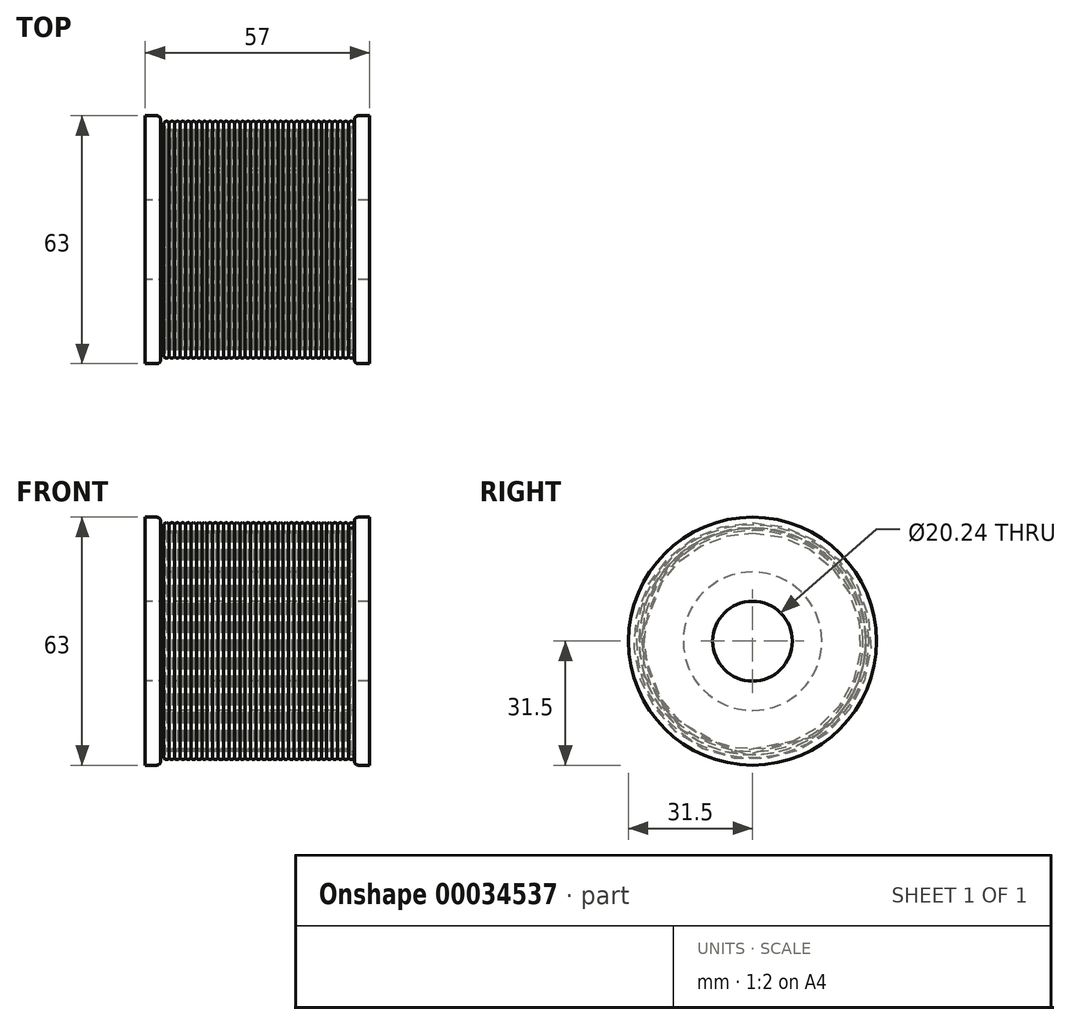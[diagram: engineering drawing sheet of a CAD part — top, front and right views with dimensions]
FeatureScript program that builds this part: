
annotation { "Feature Type Name" : "Feature", "Feature Type Description" : "" }
export const myFeature = defineFeature(function(context is Context, id is Id, definition is map)
    precondition{}
    {
        {
            var Q0;
            Q0=qCreatedBy(makeId("Front.planeOp"),FACE);
            var sketch = newSketch(context, id + "F0", { "sketchPlane" : qUnion([Q0])});
            skLineSegment(sketch, "E0", {"start": v(0, 17.6) * mm, "end": v(24.6, 17.6) * mm});
            skLineSegment(sketch, "E1", {"start": v(24.6, 17.6) * mm, "end": v(24.6, 31.5) * mm});
            skLineSegment(sketch, "E2", {"start": v(24.6, 31.5) * mm, "end": v(28.5, 31.5) * mm});
            skLineSegment(sketch, "E3", {"start": v(28.5, 31.5) * mm, "end": v(28.5, 10.12) * mm});
            skLineSegment(sketch, "E4", {"start": v(28.5, 10.12) * mm, "end": v(0, 10.12) * mm});
            skLineSegment(sketch, "E5.MirrorCS", {"start": v(0, 17.6) * mm, "end": v(-24.6, 17.6) * mm});
            skLineSegment(sketch, "E6.MirrorCS", {"start": v(-28.5, 10.12) * mm, "end": v(0, 10.12) * mm});
            skLineSegment(sketch, "E7.MirrorCS", {"start": v(-28.5, 31.5) * mm, "end": v(-28.5, 10.12) * mm});
            skLineSegment(sketch, "E8.MirrorCS", {"start": v(-24.6, 17.6) * mm, "end": v(-24.6, 31.5) * mm});
            skLineSegment(sketch, "E9.MirrorCS", {"start": v(-24.6, 31.5) * mm, "end": v(-28.5, 31.5) * mm});
            skLineSegment(sketch, "E10", {"start": v(-37.64, 0) * mm, "end": v(50.45, 0) * mm, "construction": true});
            skPoint(sketch, "E11.first.point", {"position": v(-22.46, 29.65) * mm});
            skPoint(sketch, "E11.second.point", {"position": v(-22.46, 29.64) * mm});
            skPoint(sketch, "E11.third.point", {"position": v(-22.63, 29.9) * mm});
            skArc(sketch, "E12.1.0.0", {"start": v(-21.05, 29.52) * mm, "mid": v(-21.74, 30.1) * mm, "end": v(-22.43, 29.52) * mm});
            skArc(sketch, "E12.2.0.0", {"start": v(-19.67, 29.52) * mm, "mid": v(-20.36, 30.1) * mm, "end": v(-21.05, 29.52) * mm});
            skArc(sketch, "E12.3.0.0", {"start": v(-18.29, 29.52) * mm, "mid": v(-18.98, 30.1) * mm, "end": v(-19.67, 29.52) * mm});
            skArc(sketch, "E12.4.0.0", {"start": v(-16.9, 29.52) * mm, "mid": v(-17.6, 30.1) * mm, "end": v(-18.29, 29.52) * mm});
            skArc(sketch, "E12.6.0.0", {"start": v(-14.15, 29.52) * mm, "mid": v(-14.84, 30.1) * mm, "end": v(-15.53, 29.52) * mm});
            skArc(sketch, "E12.7.0.0", {"start": v(-12.77, 29.52) * mm, "mid": v(-13.46, 30.1) * mm, "end": v(-14.15, 29.52) * mm});
            skArc(sketch, "E12.8.0.0", {"start": v(-11.39, 29.52) * mm, "mid": v(-12.08, 30.1) * mm, "end": v(-12.77, 29.52) * mm});
            skArc(sketch, "E12.9.0.0", {"start": v(-10, 29.52) * mm, "mid": v(-10.7, 30.1) * mm, "end": v(-11.39, 29.52) * mm});
            skArc(sketch, "E12.10.0.0", {"start": v(-8.63, 29.52) * mm, "mid": v(-9.32, 30.1) * mm, "end": v(-10, 29.52) * mm});
            skArc(sketch, "E12.11.0.0", {"start": v(-7.25, 29.52) * mm, "mid": v(-7.94, 30.1) * mm, "end": v(-8.63, 29.52) * mm});
            skArc(sketch, "E12.12.0.0", {"start": v(-5.87, 29.52) * mm, "mid": v(-6.56, 30.1) * mm, "end": v(-7.25, 29.52) * mm});
            skArc(sketch, "E12.13.0.0", {"start": v(-4.49, 29.52) * mm, "mid": v(-5.18, 30.1) * mm, "end": v(-5.87, 29.52) * mm});
            skArc(sketch, "E12.14.0.0", {"start": v(-3.1, 29.52) * mm, "mid": v(-3.8, 30.1) * mm, "end": v(-4.49, 29.52) * mm});
            skArc(sketch, "E12.15.0.0", {"start": v(-1.73, 29.52) * mm, "mid": v(-2.42, 30.1) * mm, "end": v(-3.1, 29.52) * mm});
            skArc(sketch, "E12.16.0.0", {"start": v(-0.35, 29.52) * mm, "mid": v(-1.04, 30.1) * mm, "end": v(-1.73, 29.52) * mm});
            skArc(sketch, "E12.17.0.0", {"start": v(1.03, 29.52) * mm, "mid": v(0.34, 30.1) * mm, "end": v(-0.35, 29.52) * mm});
            skArc(sketch, "E12.18.0.0", {"start": v(2.41, 29.52) * mm, "mid": v(1.72, 30.1) * mm, "end": v(1.03, 29.52) * mm});
            skArc(sketch, "E12.19.0.0", {"start": v(3.8, 29.52) * mm, "mid": v(3.1, 30.1) * mm, "end": v(2.41, 29.52) * mm});
            skLineSegment(sketch, "E12.direction1", {"start": v(-23.12, 29.4) * mm, "end": v(-21.74, 29.4) * mm, "construction": true});
            skArc(sketch, "E13.0.20.0", {"start": v(5.17, 29.52) * mm, "mid": v(4.48, 30.1) * mm, "end": v(3.8, 29.52) * mm});
            skArc(sketch, "E13.0.21.0", {"start": v(6.55, 29.52) * mm, "mid": v(5.86, 30.1) * mm, "end": v(5.17, 29.52) * mm});
            skArc(sketch, "E13.0.22.0", {"start": v(7.93, 29.52) * mm, "mid": v(7.24, 30.1) * mm, "end": v(6.55, 29.52) * mm});
            skArc(sketch, "E13.0.23.0", {"start": v(9.31, 29.52) * mm, "mid": v(8.62, 30.1) * mm, "end": v(7.93, 29.52) * mm});
            skArc(sketch, "E13.0.24.0", {"start": v(10.7, 29.52) * mm, "mid": v(10, 30.1) * mm, "end": v(9.31, 29.52) * mm});
            skArc(sketch, "E13.0.31.0", {"start": v(20.35, 29.52) * mm, "mid": v(19.66, 30.1) * mm, "end": v(18.97, 29.52) * mm});
            skArc(sketch, "E13.0.32.0", {"start": v(21.73, 29.52) * mm, "mid": v(21.04, 30.1) * mm, "end": v(20.35, 29.52) * mm});
            skArc(sketch, "E13.0.33.0", {"start": v(23.11, 29.52) * mm, "mid": v(22.42, 30.1) * mm, "end": v(21.73, 29.52) * mm});
            skArc(sketch, "E13.0.34.0", {"start": v(23.53, 28.76) * mm, "mid": v(24.42, 29.73) * mm, "end": v(23.11, 29.52) * mm});
            skArc(sketch, "E14.0.25.0", {"start": v(10, 28.08) * mm, "mid": v(10.7, 27.5) * mm, "end": v(11.38, 28.08) * mm});
            skArc(sketch, "E14.0.24.0", {"start": v(8.62, 28.08) * mm, "mid": v(9.31, 27.5) * mm, "end": v(10, 28.08) * mm});
            skPoint(sketch, "E15.third.point", {"position": v(-23.33, 27.68) * mm});
            skArc(sketch, "E16.16.0.0", {"start": v(-2.42, 28.08) * mm, "mid": v(-1.73, 27.5) * mm, "end": v(-1.04, 28.08) * mm});
            skArc(sketch, "E16.11.0.0", {"start": v(-9.32, 28.08) * mm, "mid": v(-8.63, 27.5) * mm, "end": v(-7.94, 28.08) * mm});
            skArc(sketch, "E14.0.26.0", {"start": v(11.38, 28.08) * mm, "mid": v(12.07, 27.5) * mm, "end": v(12.76, 28.08) * mm});
            skArc(sketch, "E16.1.0.0", {"start": v(-23.12, 28.08) * mm, "mid": v(-22.43, 27.5) * mm, "end": v(-21.74, 28.08) * mm});
            skArc(sketch, "E14.0.27.0", {"start": v(12.76, 28.08) * mm, "mid": v(13.45, 27.5) * mm, "end": v(14.14, 28.08) * mm});
            skArc(sketch, "E14.0.20.0", {"start": v(3.1, 28.08) * mm, "mid": v(3.8, 27.5) * mm, "end": v(4.48, 28.08) * mm});
            skArc(sketch, "E14.0.28.0", {"start": v(14.14, 28.08) * mm, "mid": v(14.83, 27.5) * mm, "end": v(15.52, 28.08) * mm});
            skArc(sketch, "E16.13.0.0", {"start": v(-6.56, 28.08) * mm, "mid": v(-5.87, 27.5) * mm, "end": v(-5.18, 28.08) * mm});
            skPoint(sketch, "E15.second.point", {"position": v(-23.33, 27.68) * mm});
            skArc(sketch, "E14.0.30.0", {"start": v(16.9, 28.08) * mm, "mid": v(17.6, 27.5) * mm, "end": v(18.28, 28.08) * mm});
            skPoint(sketch, "E15.first.point", {"position": v(-23.33, 27.68) * mm});
            skArc(sketch, "E15", {"start": v(-23.53, 28.84) * mm, "mid": v(-24.42, 27.86) * mm, "end": v(-23.12, 28.08) * mm});
            skLineSegment(sketch, "E16.direction1", {"start": v(-23.8, 28.2) * mm, "end": v(-22.43, 28.2) * mm, "construction": true});
            skArc(sketch, "E17.trimOffspring", {"start": v(12.07, 29.52) * mm, "mid": v(11.38, 30.1) * mm, "end": v(10.7, 29.52) * mm});
            skArc(sketch, "E18.trimOffspring", {"start": v(13.45, 29.52) * mm, "mid": v(12.76, 30.1) * mm, "end": v(12.07, 29.52) * mm});
            skArc(sketch, "E19.trimOffspring", {"start": v(14.83, 29.52) * mm, "mid": v(14.14, 30.1) * mm, "end": v(13.45, 29.52) * mm});
            skArc(sketch, "E20.trimOffspring", {"start": v(16.21, 29.52) * mm, "mid": v(15.52, 30.1) * mm, "end": v(14.83, 29.52) * mm});
            skArc(sketch, "E21.trimOffspring", {"start": v(15.52, 28.08) * mm, "mid": v(16.21, 27.5) * mm, "end": v(16.9, 28.08) * mm});
            skArc(sketch, "E22.trimOffspring", {"start": v(17.6, 29.52) * mm, "mid": v(16.9, 30.1) * mm, "end": v(16.21, 29.52) * mm});
            skArc(sketch, "E23.trimOffspring", {"start": v(22.42, 28.08) * mm, "mid": v(23.48, 27.6) * mm, "end": v(23.53, 28.76) * mm});
            skArc(sketch, "E24.trimOffspring", {"start": v(21.04, 28.08) * mm, "mid": v(21.73, 27.5) * mm, "end": v(22.42, 28.08) * mm});
            skArc(sketch, "E25.trimOffspring", {"start": v(19.66, 28.08) * mm, "mid": v(20.35, 27.5) * mm, "end": v(21.04, 28.08) * mm});
            skArc(sketch, "E26.trimOffspring", {"start": v(18.97, 29.52) * mm, "mid": v(18.28, 30.1) * mm, "end": v(17.6, 29.52) * mm});
            skArc(sketch, "E27.trimOffspring", {"start": v(18.28, 28.08) * mm, "mid": v(18.97, 27.5) * mm, "end": v(19.66, 28.08) * mm});
            skArc(sketch, "E28.trimOffspring", {"start": v(7.24, 28.08) * mm, "mid": v(7.93, 27.5) * mm, "end": v(8.62, 28.08) * mm});
            skArc(sketch, "E29.trimOffspring", {"start": v(5.86, 28.08) * mm, "mid": v(6.55, 27.5) * mm, "end": v(7.24, 28.08) * mm});
            skArc(sketch, "E30.trimOffspring", {"start": v(4.48, 28.08) * mm, "mid": v(5.17, 27.5) * mm, "end": v(5.86, 28.08) * mm});
            skArc(sketch, "E31.trimOffspring", {"start": v(1.72, 28.08) * mm, "mid": v(2.41, 27.5) * mm, "end": v(3.1, 28.08) * mm});
            skArc(sketch, "E32.trimOffspring", {"start": v(0.34, 28.08) * mm, "mid": v(1.03, 27.5) * mm, "end": v(1.72, 28.08) * mm});
            skArc(sketch, "E33.trimOffspring", {"start": v(-1.04, 28.08) * mm, "mid": v(-0.35, 27.5) * mm, "end": v(0.34, 28.08) * mm});
            skArc(sketch, "E34.trimOffspring", {"start": v(-3.8, 28.08) * mm, "mid": v(-3.1, 27.5) * mm, "end": v(-2.42, 28.08) * mm});
            skArc(sketch, "E35.trimOffspring", {"start": v(-5.18, 28.08) * mm, "mid": v(-4.49, 27.5) * mm, "end": v(-3.8, 28.08) * mm});
            skArc(sketch, "E36.trimOffspring", {"start": v(-7.94, 28.08) * mm, "mid": v(-7.25, 27.5) * mm, "end": v(-6.56, 28.08) * mm});
            skArc(sketch, "E37.trimOffspring", {"start": v(-10.7, 28.08) * mm, "mid": v(-10, 27.5) * mm, "end": v(-9.32, 28.08) * mm});
            skArc(sketch, "E38.trimOffspring", {"start": v(-12.08, 28.08) * mm, "mid": v(-11.39, 27.5) * mm, "end": v(-10.7, 28.08) * mm});
            skArc(sketch, "E39.trimOffspring", {"start": v(-16.22, 28.08) * mm, "mid": v(-15.53, 27.5) * mm, "end": v(-14.84, 28.08) * mm});
            skArc(sketch, "E40.trimOffspring", {"start": v(-18.98, 28.08) * mm, "mid": v(-18.29, 27.5) * mm, "end": v(-17.6, 28.08) * mm});
            skArc(sketch, "E41.trimOffspring", {"start": v(-14.84, 28.08) * mm, "mid": v(-14.15, 27.5) * mm, "end": v(-13.46, 28.08) * mm});
            skArc(sketch, "E42.trimOffspring", {"start": v(-13.46, 28.08) * mm, "mid": v(-12.77, 27.5) * mm, "end": v(-12.08, 28.08) * mm});
            skArc(sketch, "E43.trimOffspring", {"start": v(-17.6, 28.08) * mm, "mid": v(-16.9, 27.5) * mm, "end": v(-16.22, 28.08) * mm});
            skArc(sketch, "E44.trimOffspring", {"start": v(-15.53, 29.52) * mm, "mid": v(-16.22, 30.1) * mm, "end": v(-16.9, 29.52) * mm});
            skArc(sketch, "E45.trimOffspring", {"start": v(-20.36, 28.08) * mm, "mid": v(-19.67, 27.5) * mm, "end": v(-18.98, 28.08) * mm});
            skArc(sketch, "E46.trimOffspring", {"start": v(-21.74, 28.08) * mm, "mid": v(-21.05, 27.5) * mm, "end": v(-20.36, 28.08) * mm});
            skArc(sketch, "E47.trimOffspring", {"start": v(-22.43, 29.52) * mm, "mid": v(-23.48, 30) * mm, "end": v(-23.53, 28.84) * mm});
            skSolve(sketch);
        }
        {
            var Q0;
            Q0=makeQuery(id+"F0.imprint","IMPRINT",FACE,{"disambiguationData":[TD([[makeQuery(id+"F0.imprint","IMPRINT",EDGE,{"derivedFrom":sQuery(id+"F0.wireOp",EDGE,"E12.1.0.0")}),1.0]])]});
            var Q1;
            Q1=sQuery(id+"F0.wireOp",EDGE,"E10");
            revolve(context, id + "F1", {"entities" : qUnion([Q0]), "axis" : qUnion([Q1]), "revolveType" : RevolveType.FULL});
        }
        {
            var Q0;
            Q0=makeQuery(id+"F0.imprint","IMPRINT",FACE,{"disambiguationData":[TD([[makeQuery(id+"F0.imprint","IMPRINT",EDGE,{"derivedFrom":sQuery(id+"F0.wireOp",EDGE,"E0")}),-1.0]])]});
            var Q1;
            Q1=sQuery(id+"F0.wireOp",EDGE,"E10");
            revolve(context, id + "F2", {"entities" : qUnion([Q0]), "axis" : qUnion([Q1]), "revolveType" : RevolveType.FULL});
        }
        {
            var Q0;
            Q0=makeQuery(id+"F2.opRevolve","SWEPT_EDGE",EDGE,{"disambiguationData":[OSD([sQuery(id+"F0.wireOp",EDGE,"E8.MirrorCS"),sQuery(id+"F0.wireOp",EDGE,"E9.MirrorCS")])]});
            var Q1;
            Q1=makeQuery(id+"F2.opRevolve","SWEPT_EDGE",EDGE,{"disambiguationData":[OSD([sQuery(id+"F0.wireOp",EDGE,"E1"),sQuery(id+"F0.wireOp",EDGE,"E2")])]});
            fillet(context, id + "F3", {"entities" : qUnion([Q0, Q1]), "radius" : 1 * mm, "tangentPropagation" : true, "allowEdgeOverflow" : false});
        }
    });
